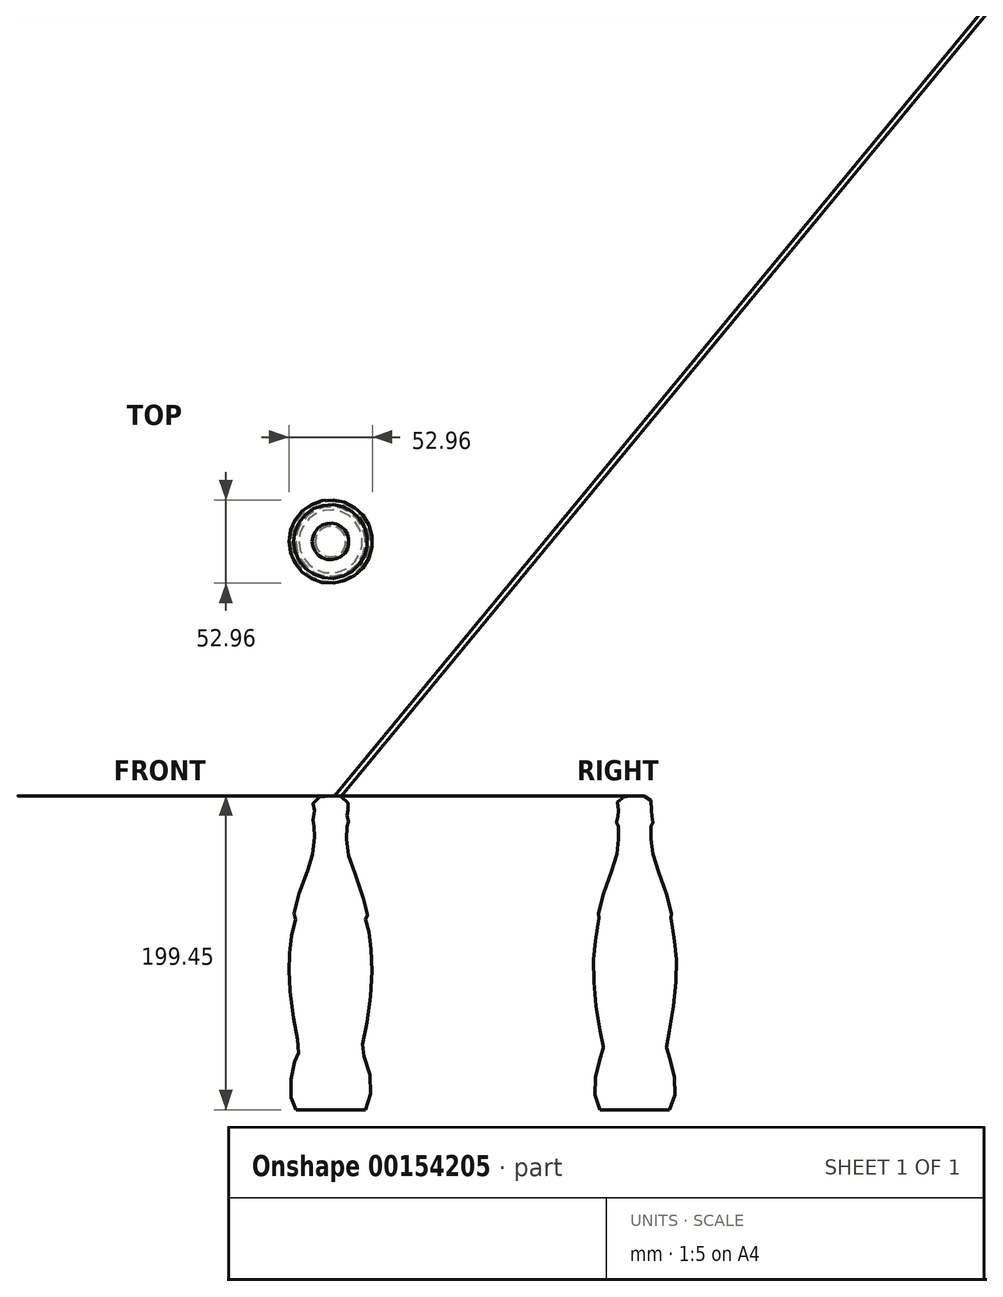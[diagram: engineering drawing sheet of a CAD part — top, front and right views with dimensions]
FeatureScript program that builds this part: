
annotation { "Feature Type Name" : "Feature", "Feature Type Description" : "" }
export const myFeature = defineFeature(function(context is Context, id is Id, definition is map)
    precondition{}
    {
        {
            var Q0;
            Q0=qCreatedBy(makeId("Front.planeOp"),FACE);
            var sketch = newSketch(context, id + "F0", { "sketchPlane" : qUnion([Q0])});
            skPoint(sketch, "E0", {"position": v(0, 0) * mm});
            skLineSegment(sketch, "E1", {"start": v(0, -100) * mm, "end": v(-22.08, -100) * mm});
            skFitSpline(sketch, "E2", {"points": [v(-22.08, -100) * mm, v(-24.48, -96.17) * mm, v(-25.4, -86.49) * mm, v(-24.57, -75.57) * mm, v(-22.08, -67.46) * mm, v(-21, -65.64) * mm, v(-20.1, -62.24) * mm, v(-20.76, -56.12) * mm, v(-23.57, -41.06) * mm, v(-26.14, -21.61) * mm, v(-26.14, -18.55) * mm, v(-25.64, -16.23) * mm, v(-25.48, -15.57) * mm, v(-26.22, -12.5) * mm, v(-26.14, -1.83) * mm, v(-25.06, 7.52) * mm, v(-22.83, 19.52) * mm, v(-22.08, 21.42) * mm, v(-23.08, 22) * mm, v(-23.4, 23.49) * mm, v(-20.84, 34.41) * mm, v(-14.64, 52.04) * mm, v(-11.57, 61.3) * mm, v(-10.42, 69.83) * mm, v(-9.88, 79.46) * mm, v(-9.9, 79.68) * mm, v(-10.08, 79.77) * mm, v(-11.24, 80.56) * mm, v(-11.57, 81.24) * mm, v(-11.5, 83.17) * mm, v(-9.87, 89.17) * mm, v(-9.75, 89.8) * mm, v(-10.8, 90.23) * mm, v(-11.55, 91.16) * mm, v(-11.42, 93.82) * mm, v(-10.24, 96.43) * mm, v(-7.64, 98.35) * mm, v(-5.16, 99.28) * mm, v(0, 99.4) * mm], "startDerivative": vector(-104.34, 123.1) * mm, "endDerivative": vector(202.6, -5.96) * mm});
            skLineSegment(sketch, "E3", {"start": v(0, -100) * mm, "end": v(0, 100) * mm});
            skSolve(sketch);
        }
        {
            var Q0;
            {var subQ0=sQuery(id+"F0.wireOp",EDGE,"E1");Q0=makeQuery(id+"F0.imprint","IMPRINT",FACE,{"disambiguationData":[TD([[makeQuery(id+"F0.imprint","IMPRINT",EDGE,{"derivedFrom":subQ0}),-1.0]])]});}
            var Q1;
            Q1=sQuery(id+"F0.wireOp",EDGE,"E3");
            revolve(context, id + "F1", {"entities" : qUnion([Q0]), "axis" : qUnion([Q1]), "revolveType" : RevolveType.FULL});
        }
    });
